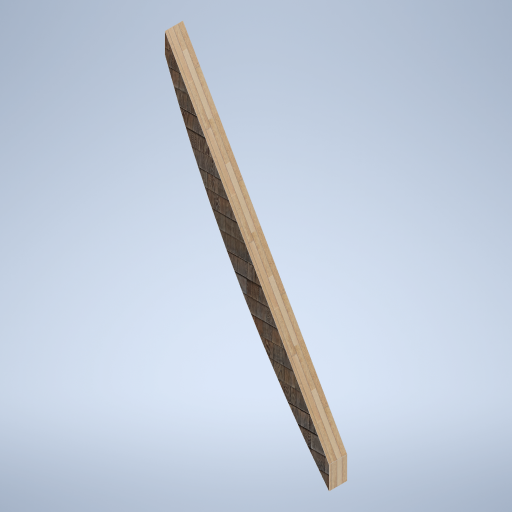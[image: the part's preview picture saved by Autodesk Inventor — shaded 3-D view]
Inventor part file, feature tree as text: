
AUTODESK INVENTOR PART (.ipt)
format: ipt  version: 2024.2 (Build 282272000, 272)  size: 303,616 bytes
history: native  units: in
note: dims shown in document units (in); Inventor stores cm internally (conversion verified against a paired STEP export)
features: other x3, sketch x1
ambient origin geometry x8: Origin, YZ Plane, XZ Plane, XY Plane, X Axis, Y Axis, Z Axis, Center Point
bodies: Body1 (feature_tree)
feature tree (4):
  other  "side_curve_beam_04_MIR.ipt"
  other  "Solid2::side_curve_beam_04_MIR.ipt"
  other  "TaggingFeature1"
  sketch  "Sketch1"  dims[d0=0.3937in]
